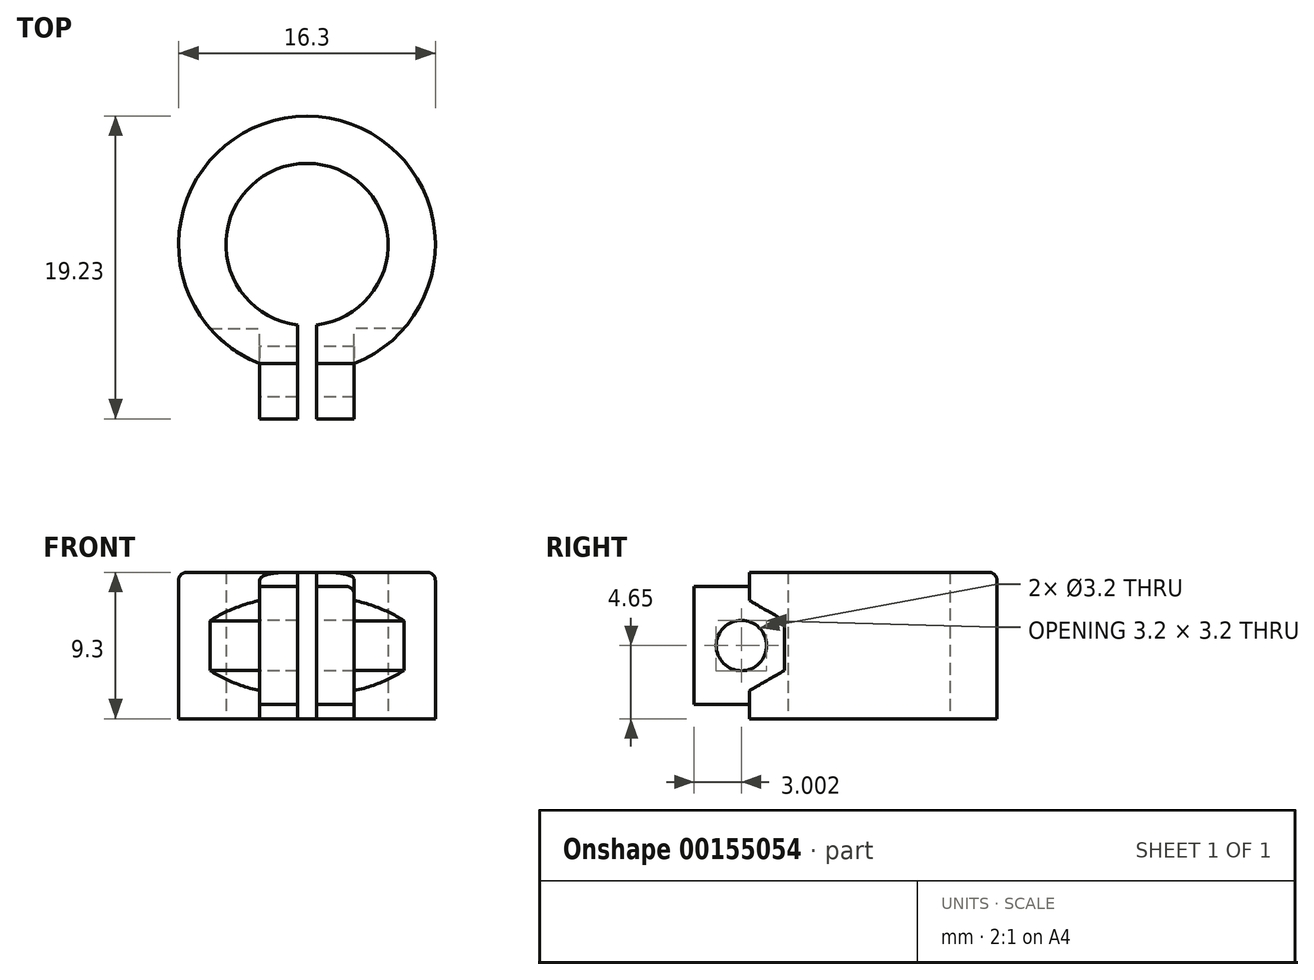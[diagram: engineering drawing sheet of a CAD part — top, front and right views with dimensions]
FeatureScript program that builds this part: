
annotation { "Feature Type Name" : "Feature", "Feature Type Description" : "" }
export const myFeature = defineFeature(function(context is Context, id is Id, definition is map)
    precondition{}
    {
        {
            var Q0;
            Q0=qCreatedBy(makeId("Top.planeOp"),FACE);
            var sketch = newSketch(context, id + "F0", { "sketchPlane" : qUnion([Q0])});
            skCircle(sketch, "E0", {"center": v(0, 0) * mm, "radius": 5.15 * mm});
            skCircle(sketch, "E1", {"center": v(0, 0) * mm, "radius": 8.15 * mm});
            skLineSegment(sketch, "E2.bottom", {"start": v(-3, -11.08) * mm, "end": v(3, -11.08) * mm});
            skLineSegment(sketch, "E2.top", {"start": v(-3, -7.58) * mm, "end": v(3, -7.58) * mm});
            skLineSegment(sketch, "E2.left", {"start": v(-3, -11.08) * mm, "end": v(-3, -7.58) * mm});
            skLineSegment(sketch, "E2.right", {"start": v(3, -11.08) * mm, "end": v(3, -7.58) * mm});
            skPoint(sketch, "E3", {"position": v(0, -8.15) * mm});
            skPoint(sketch, "E4", {"position": v(0, -7.58) * mm});
            skSolve(sketch);
        }
        {
            var Q0;
            Q0 = qSketchRegion(id + "F0", true);
            extrude(context, id + "F1", {"entities" : qUnion([Q0]), "depth" : 9.3 * mm});
        }
        {
            var Q0;
            Q0=qCreatedBy(makeId("Top.planeOp"),FACE);
            var sketch = newSketch(context, id + "F2", { "sketchPlane" : qUnion([Q0])});
            skLineSegment(sketch, "E5.bottom", {"start": v(-0.6, 0) * mm, "end": v(0.6, 0) * mm});
            skLineSegment(sketch, "E5.top", {"start": v(-0.6, -13.86) * mm, "end": v(0.6, -13.86) * mm});
            skLineSegment(sketch, "E5.left", {"start": v(-0.6, 0) * mm, "end": v(-0.6, -13.86) * mm});
            skLineSegment(sketch, "E5.right", {"start": v(0.6, 0) * mm, "end": v(0.6, -13.86) * mm});
            skSolve(sketch);
        }
        {
            var Q0;
            Q0 = qSketchRegion(id + "F2", true);
            extrude(context, id + "F3", {"entities" : qUnion([Q0]), "operationType" : NewBodyOperationType.REMOVE, "endBound" : BoundingType.THROUGH_ALL, "depth" : 25 * mm});
        }
        {
            var Q0;
            Q0=makeQuery(id+"F1.opExtrude","SWEPT_FACE",FACE,{"disambiguationData":[OSD([sQuery(id+"F0.wireOp",EDGE,"E2.left")])]});
            var sketch = newSketch(context, id + "F4", { "sketchPlane" : qUnion([Q0])});
            skLineSegment(sketch, "E6.0", {"start": v(11.08, 9.3) * mm, "end": v(7.58, 9.3) * mm, "construction": true});
            skLineSegment(sketch, "E7.0", {"start": v(7.58, 9.3) * mm, "end": v(7.58, 0) * mm, "construction": true});
            skLineSegment(sketch, "E8.0", {"start": v(11.08, 9.3) * mm, "end": v(11.08, 0) * mm, "construction": true});
            skLineSegment(sketch, "E9.0", {"start": v(11.08, 0) * mm, "end": v(7.58, 0) * mm, "construction": true});
            skLineSegment(sketch, "E10.bottom", {"start": v(7.58, 8.4) * mm, "end": v(11.08, 8.4) * mm});
            skLineSegment(sketch, "E10.top", {"start": v(7.58, 0.9) * mm, "end": v(11.08, 0.9) * mm});
            skLineSegment(sketch, "E10.left", {"start": v(7.58, 8.4) * mm, "end": v(7.58, 0.9) * mm});
            skLineSegment(sketch, "E10.right", {"start": v(11.08, 8.4) * mm, "end": v(11.08, 0.9) * mm});
            skPoint(sketch, "E11", {"position": v(7.58, 4.65) * mm});
            skSolve(sketch);
        }
        {
            var Q0;
            {var subQ0=sQuery(id+"F4.wireOp",EDGE,"E10.bottom");Q0=makeQuery(id+"F4.imprint","IMPRINT",FACE,{"disambiguationData":[TD([[makeQuery(id+"F4.imprint","IMPRINT",EDGE,{"derivedFrom":subQ0}),1.0]])]});}
            var Q1;
            {var subQ0=sQuery(id+"F4.wireOp",EDGE,"E10.top");Q1=makeQuery(id+"F4.imprint","IMPRINT",FACE,{"disambiguationData":[TD([[makeQuery(id+"F4.imprint","IMPRINT",EDGE,{"derivedFrom":subQ0}),-1.0]])]});}
            extrude(context, id + "F5", {"entities" : qUnion([Q0, Q1]), "operationType" : NewBodyOperationType.REMOVE, "oppositeDirection" : true, "depth" : 25 * mm});
        }
        {
            var Q0;
            Q0=makeQuery(id+"F1.opExtrude","SWEPT_FACE",FACE,{"disambiguationData":[OSD([sQuery(id+"F0.wireOp",EDGE,"E2.left")])]});
            cPlane(context, id + "F6", {"entities" : qUnion([Q0]), "cplaneType" : CPlaneType.OFFSET, "offset" : 10 * mm, "width" : 150 * mm, "height" : 150 * mm});
        }
        {
            var Q0;
            Q0=qCreatedBy(id+"F6.planeOp",FACE);
            var sketch = newSketch(context, id + "F7", { "sketchPlane" : qUnion([Q0])});
            skCircle(sketch, "E12", {"center": v(8.08, 4.65) * mm, "radius": 1.6 * mm});
            skPoint(sketch, "E13", {"position": v(11.08, 4.65) * mm});
            skSolve(sketch);
        }
        {
            var Q0;
            Q0 = qSketchRegion(id + "F7", true);
            extrude(context, id + "F8", {"entities" : qUnion([Q0]), "operationType" : NewBodyOperationType.REMOVE, "endBound" : BoundingType.THROUGH_ALL, "oppositeDirection" : true, "depth" : 25 * mm});
        }
        {
            var Q0;
            Q0=makeQuery(id+"F1.opExtrude","SWEPT_FACE",FACE,{"disambiguationData":[OSD([sQuery(id+"F0.wireOp",EDGE,"E2.left")])]});
            var sketch = newSketch(context, id + "F9", { "sketchPlane" : qUnion([Q0])});
            skArc(sketch, "E14.0", {"start": v(7.58, 3.13) * mm, "mid": v(9.68, 4.65) * mm, "end": v(7.58, 6.17) * mm, "construction": true});
            skCircle(sketch, "E15.cCircle", {"center": v(8.08, 4.65) * mm, "radius": 2.74 * mm, "construction": true});
            skLineSegment(sketch, "E15.0", {"start": v(8.08, 7.8) * mm, "end": v(10.81, 6.23) * mm});
            skLineSegment(sketch, "E15.1", {"start": v(10.81, 6.23) * mm, "end": v(10.81, 3.07) * mm});
            skLineSegment(sketch, "E15.2", {"start": v(10.81, 3.07) * mm, "end": v(8.08, 1.5) * mm});
            skLineSegment(sketch, "E15.3", {"start": v(8.08, 1.5) * mm, "end": v(5.34, 3.07) * mm});
            skLineSegment(sketch, "E15.4", {"start": v(5.34, 3.07) * mm, "end": v(5.34, 6.23) * mm});
            skLineSegment(sketch, "E15.5", {"start": v(5.34, 6.23) * mm, "end": v(8.08, 7.8) * mm});
            skPoint(sketch, "E15.0.midPoint", {"position": v(9.45, 7.02) * mm});
            skSolve(sketch);
        }
        {
            var Q0;
            Q0 = qSketchRegion(id + "F9", true);
            var Q1;
            Q1 = qConstructionFilter(qBodyType(qCreatedBy(id + "F9" ,EDGE), BodyType.WIRE), ConstructionObject.NO);
            extrude(context, id + "F10", {"entities" : qUnion([Q0]), "operationType" : NewBodyOperationType.REMOVE, "surfaceEntities" : qUnion([Q1]), "depth" : 25 * mm});
        }
        {
            var Q0;
            Q0=makeQuery(id+"F1.opExtrude","SWEPT_FACE",FACE,{"disambiguationData":[OSD([sQuery(id+"F0.wireOp",EDGE,"E2.right")])]});
            var sketch = newSketch(context, id + "F11", { "sketchPlane" : qUnion([Q0])});
            skLineSegment(sketch, "E16.0", {"start": v(-5.34, 6.23) * mm, "end": v(-8.08, 7.8) * mm});
            skLineSegment(sketch, "E16.1", {"start": v(-8.08, 1.5) * mm, "end": v(-5.34, 3.07) * mm});
            skLineSegment(sketch, "E16.2", {"start": v(-5.34, 3.07) * mm, "end": v(-5.34, 6.23) * mm});
            skLineSegment(sketch, "E16.3", {"start": v(-8.08, 7.8) * mm, "end": v(-10.81, 6.23) * mm});
            skLineSegment(sketch, "E16.4", {"start": v(-10.81, 6.23) * mm, "end": v(-10.81, 3.07) * mm});
            skLineSegment(sketch, "E16.5", {"start": v(-10.81, 3.07) * mm, "end": v(-8.08, 1.5) * mm});
            skSolve(sketch);
        }
        {
            var Q0;
            Q0 = qSketchRegion(id + "F11", true);
            extrude(context, id + "F12", {"entities" : qUnion([Q0]), "operationType" : NewBodyOperationType.REMOVE, "depth" : 25 * mm});
        }
        {
            var Q0;
            Q0=makeQuery(id+"F1.opExtrude","CAP_EDGE",EDGE,{"disambiguationData":[OSD([sQuery(id+"F0.wireOp",EDGE,"E1")])],"isStart":false});
            var Q1;
            {var subQ0=sQuery(id+"F0.wireOp",EDGE,"E2.left");var subQ1=sQuery(id+"F0.wireOp",EDGE,"E1");var subQ2=sQuery(id+"F0.wireOp",EDGE,"E2.top");var subQ3=makeQuery(id+"F1.opExtrude","SWEPT_EDGE",EDGE,{"disambiguationData":[OSD([subQ1,subQ2,subQ0])]});var subQ4=makeQuery(id+"F4.imprint","INTERSECT",VERTEX,{"derivedFrom":[subQ3,makeQuery(id+"F1.opExtrude","CAP_EDGE",EDGE,{"disambiguationData":[OSD([subQ0])],"isStart":false})]});Q1=makeQuery(id+"F5.boolean.opBoolean","COPY",EDGE,{"disambiguationData":[TD([makeQuery(id+"F3.boolean.opBoolean","COPY",FACE,{"derivedFrom":makeQuery(id+"F3.opExtrude","SWEPT_FACE",FACE,{"disambiguationData":[OSD([sQuery(id+"F2.wireOp",EDGE,"E5.right")])]})})])],"derivedFrom":makeQuery(id+"F5.opExtrude","SWEPT_EDGE",EDGE,{"disambiguationData":[OSD([subQ1,subQ2,subQ0]),TDD([subQ4])]})});}
            var Q2;
            {var subQ0=sQuery(id+"F0.wireOp",EDGE,"E2.left");var subQ1=sQuery(id+"F0.wireOp",EDGE,"E1");var subQ2=sQuery(id+"F0.wireOp",EDGE,"E2.top");var subQ3=makeQuery(id+"F1.opExtrude","SWEPT_EDGE",EDGE,{"disambiguationData":[OSD([subQ1,subQ2,subQ0])]});var subQ4=makeQuery(id+"F4.imprint","INTERSECT",VERTEX,{"derivedFrom":[subQ3,makeQuery(id+"F1.opExtrude","CAP_EDGE",EDGE,{"disambiguationData":[OSD([subQ0])],"isStart":false})]});Q2=makeQuery(id+"F5.boolean.opBoolean","COPY",EDGE,{"disambiguationData":[TD([makeQuery(id+"F3.boolean.opBoolean","COPY",FACE,{"derivedFrom":makeQuery(id+"F3.opExtrude","SWEPT_FACE",FACE,{"disambiguationData":[OSD([sQuery(id+"F2.wireOp",EDGE,"E5.left")])]})})])],"derivedFrom":makeQuery(id+"F5.opExtrude","SWEPT_EDGE",EDGE,{"disambiguationData":[OSD([subQ1,subQ2,subQ0]),TDD([subQ4])]})});}
            var Q3;
            {var subQ0=sQuery(id+"F0.wireOp",EDGE,"E2.bottom");var subQ1=sQuery(id+"F4.wireOp",EDGE,"E10.bottom");Q3=makeQuery(id+"F5.boolean.opBoolean","COPY",EDGE,{"disambiguationData":[TD([makeQuery(id+"F1.opExtrude","SWEPT_FACE",FACE,{"disambiguationData":[OSD([sQuery(id+"F0.wireOp",EDGE,"E2.right")])]})])],"derivedFrom":makeQuery(id+"F5.opExtrude","SWEPT_EDGE",EDGE,{"disambiguationData":[OSD([subQ0,sQuery(id+"F0.wireOp",EDGE,"E2.left"),subQ1,sQuery(id+"F4.wireOp",EDGE,"E10.right")])]})});}
            var Q4;
            {var subQ0=sQuery(id+"F0.wireOp",EDGE,"E2.bottom");var subQ1=sQuery(id+"F0.wireOp",EDGE,"E2.left");var subQ2=sQuery(id+"F4.wireOp",EDGE,"E10.bottom");Q4=makeQuery(id+"F5.boolean.opBoolean","COPY",EDGE,{"disambiguationData":[TD([makeQuery(id+"F1.opExtrude","SWEPT_FACE",FACE,{"disambiguationData":[OSD([subQ1])]})])],"derivedFrom":makeQuery(id+"F5.opExtrude","SWEPT_EDGE",EDGE,{"disambiguationData":[OSD([subQ0,subQ1,subQ2,sQuery(id+"F4.wireOp",EDGE,"E10.right")])]})});}
            var Q5;
            Q5=makeQuery(id+"F5.boolean.opBoolean","INTERSECT",EDGE,{"derivedFrom":[makeQuery(id+"F1.opExtrude","SWEPT_FACE",FACE,{"disambiguationData":[OSD([sQuery(id+"F0.wireOp",EDGE,"E2.right")])]}),makeQuery(id+"F5.opExtrude","SWEPT_FACE",FACE,{"disambiguationData":[OSD([sQuery(id+"F4.wireOp",EDGE,"E10.bottom")])]})]});
            var Q6;
            Q6=makeQuery(id+"F5.boolean.opBoolean","COPY",EDGE,{"derivedFrom":makeQuery(id+"F5.opExtrude","CAP_EDGE",EDGE,{"disambiguationData":[OSD([sQuery(id+"F4.wireOp",EDGE,"E10.bottom")])],"isStart":true})});
            fillet(context, id + "F13", {"entities" : qUnion([Q0, Q1, Q2, Q3, Q4, Q5, Q6]), "radius" : 0.5 * mm, "tangentPropagation" : true, "allowEdgeOverflow" : false});
        }
    });
